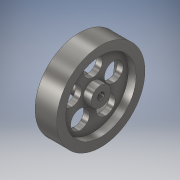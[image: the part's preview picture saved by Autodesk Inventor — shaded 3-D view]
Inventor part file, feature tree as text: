
AUTODESK INVENTOR PART (.ipt)
format: ipt  version: 2018 (Build 220112000, 112)  size: 159,744 bytes
history: native  units: in
note: dims shown in document units (in); Inventor stores cm internally (conversion verified against a paired STEP export)
features: sketch x2, revolve x1, thread x1, extrude x1
ambient origin geometry x8: Origin, YZ Plane, XZ Plane, XY Plane, X Axis, Y Axis, Z Axis, Center Point
bodies: Body1 (feature_tree)
feature tree (5):
  revolve  "Revolution1"  [1 undecoded]
  thread  "Thread1"  [1 undecoded]
  extrude  "Extrusion3"  Depth=0.1in
  sketch  "Sketch3"  dims[d10=0.045in d11=0.274in d12=0.077in]
  sketch  "Sketch4"  dims[d13=0.1in d14=0.1in d15=0.323in d16=0.112in d17=90.0deg d18=1.0in d19=0.0in d20=0.239in d21=1.9685in d23=360.0deg d25=0.275in d26=0.0in]
note: 2 required parameter values undecoded (feature->parameter linkage not recoverable at this tier; creation-order binding heuristic only, values carry confidence <= 0.55)